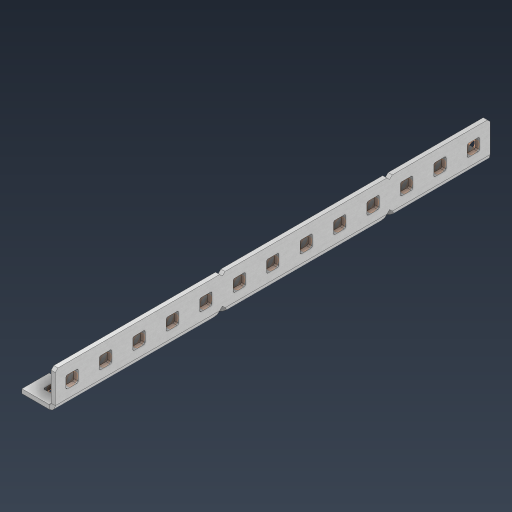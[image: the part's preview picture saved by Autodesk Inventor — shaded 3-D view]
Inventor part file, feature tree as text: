
AUTODESK INVENTOR PART (.ipt)
format: ipt  version: 2024.3 (Build 283343000, 343)  size: 671,744 bytes
history: native  units: in
note: dims shown in document units (in); Inventor stores cm internally (conversion verified against a paired STEP export)
features: other x46, extrude x37, sheet_metal_op x11, pattern_linear x2, mirror x1, chamfer x1, sketch x1
ambient origin geometry x8: Origin, YZ Plane, XZ Plane, XY Plane, X Axis, Y Axis, Z Axis, Center Point
bodies: Solid1 (feature_tree), Body (feature_tree)
feature tree (99):
  sheet_metal_op  "Flanges"
  other  "Flange Pattern Plane"
  other  "Flange Pattern Sketch"
  sheet_metal_op  "Flange Pattern"
  sheet_metal_op  "Body Pattern"
  pattern_linear  "Center Pattern"  Spacing1=6.5in  [1 undecoded]
  other  "Arc Length"
  mirror  "Notch Mirror"
  pattern_linear  "Notch Pattern"  Spacing1=0.0625in  [1 undecoded]
  chamfer  "End Chamfer"
  extrude  "Half Cut"  Depth=0.0625in
  other  "Plate1"
  sketch  "Sketch2"  dims[d0=1.0in d1=6.5in d2=0.0625in d3=0.0625in d4=0.0312in d5=0.125in d6=0.0625in d7=0.5in d8=90.0deg d9=0.0312in d10=0.25in d11=0.0625in d12=0.0625in d16=0.182in d17=0.02in d18=0.0625in d19=0.0in d20=0.25in d21=0.25in d38=5.1181in d40=0.5in d41=0.3937in d43=1.0in d46=0.172in d47=1.0in d48=0.0in d49=0.182in d50=0.02in d51=0.25in d52=0.25in d53=0.0625in d54=0.0in d55=0.172in d56=1.0in d57=0.0in d58=0.25in d60=5.1181in d62=0.5in d63=0.3937in d65=0.5in d85=0.1473in d86=0.1782in d88=0.04in d89=0.0625in d90=0.0in d91=0.04in d92=0.0491in d95=2.5in d96=0.04in d97=0.25in d98=45.0deg d99=0.25in d100=0.5in d101=0.0in d102=2.497in d106=0.182in d107=0.02in d108=0.5in d109=0.5in d110=0.0625in d111=0.0in d112=0.172in d113=0.5in d114=0.0in d117=0.5in d118=0.5in d119=0.5in]
  other  "Plate2"
  sheet_metal_op  "Bend1"
  sheet_metal_op  "Corner1"
  other  "Srf1"
  other  "Srf2"
  other  "Srf91"
  sheet_metal_op  "Body Pattern Sketch"
  other  "Srf92"
  other  "Srf786"
  other  "Srf823"
  other  "Srf824"
  other  "Srf825"
  other  "Srf826"
  other  "Srf827"
  other  "Srf828"
  other  "Srf829"
  other  "Srf856"
  other  "Srf857"
  other  "Srf858"
  other  "Srf859"
  other  "Srf860"
  other  "Srf861"
  other  "Srf862"
  other  "Srf889"
  other  "Srf890"
  other  "Srf891"
  other  "Srf892"
  other  "Srf893"
  other  "Srf894"
  other  "Srf895"
  other  "Srf896"
  other  "Srf922"
  other  "Srf923"
  other  "Srf924"
  other  "Srf925"
  other  "Srf959"
  other  "Srf960"
  other  "Srf961"
  other  "Srf962"
  other  "Srf996"
  other  "Srf997"
  other  "Srf998"
  other  "Srf999"
  sheet_metal_op  "Flange Stamp"
  sheet_metal_op  "Flange Circle"
  sheet_metal_op  "Body Stamp"
  sheet_metal_op  "Body Circle"
  other  "Center Stamp"
  other  "Center Circle"
  sheet_metal_op  "Notch"
  extrude  "ExtrusionSrf2"  Depth=0.0312in
  extrude  "ExtrusionSrf92"  Depth=0.5in
  extrude  "ExtrusionSrf823"  Depth=0.0625in
  extrude  "ExtrusionSrf824"  Depth=0.5in TaperAngle=90.0deg
  extrude  "ExtrusionSrf825"  Depth=0.5in
  extrude  "ExtrusionSrf826"  Depth=0.0625in
  extrude  "ExtrusionSrf827"  Depth=0.0625in
  extrude  "ExtrusionSrf828"  Depth=0.182in
  extrude  "ExtrusionSrf829"  Depth=0.02in
  extrude  "ExtrusionSrf856"  Depth=0.0625in
  extrude  "ExtrusionSrf857"  TaperAngle=0.0deg  [1 undecoded]
  extrude  "ExtrusionSrf858"  Depth=0.5in
  extrude  "ExtrusionSrf859"  Depth=0.5in
  extrude  "ExtrusionSrf860"  Depth=0.5in
  extrude  "ExtrusionSrf861"  Depth=0.5in
  extrude  "ExtrusionSrf862"  Depth=1.0in TaperAngle=0.0deg
  extrude  "ExtrusionSrf889"  Depth=0.182in
  extrude  "ExtrusionSrf890"  Depth=0.02in
  extrude  "ExtrusionSrf891"  Depth=0.5in
  extrude  "ExtrusionSrf892"  Depth=0.5in
  extrude  "ExtrusionSrf893"  Depth=0.0625in
  extrude  "ExtrusionSrf894"  TaperAngle=0.0deg  [1 undecoded]
  extrude  "ExtrusionSrf895"  Depth=0.5in
  extrude  "ExtrusionSrf896"  Depth=1.0in TaperAngle=0.0deg
  extrude  "ExtrusionSrf922"  Depth=0.5in
  extrude  "ExtrusionSrf923"  Depth=0.5in
  extrude  "ExtrusionSrf924"  Depth=0.5in
  extrude  "ExtrusionSrf925"  Depth=0.5in
  extrude  "ExtrusionSrf959"  Depth=0.5in
  extrude  "ExtrusionSrf960"  Depth=0.5in
  extrude  "ExtrusionSrf961"  Depth=0.0625in
  extrude  "ExtrusionSrf962"  TaperAngle=0.0deg  [1 undecoded]
  extrude  "ExtrusionSrf996"  Depth=0.5in
  extrude  "ExtrusionSrf997"  Depth=0.5in
  extrude  "ExtrusionSrf998"  Depth=2.5in
  extrude  "ExtrusionSrf999"  Depth=0.5in TaperAngle=45.0deg
note: 5 required parameter values undecoded (feature->parameter linkage not recoverable at this tier; creation-order binding heuristic only, values carry confidence <= 0.55)
